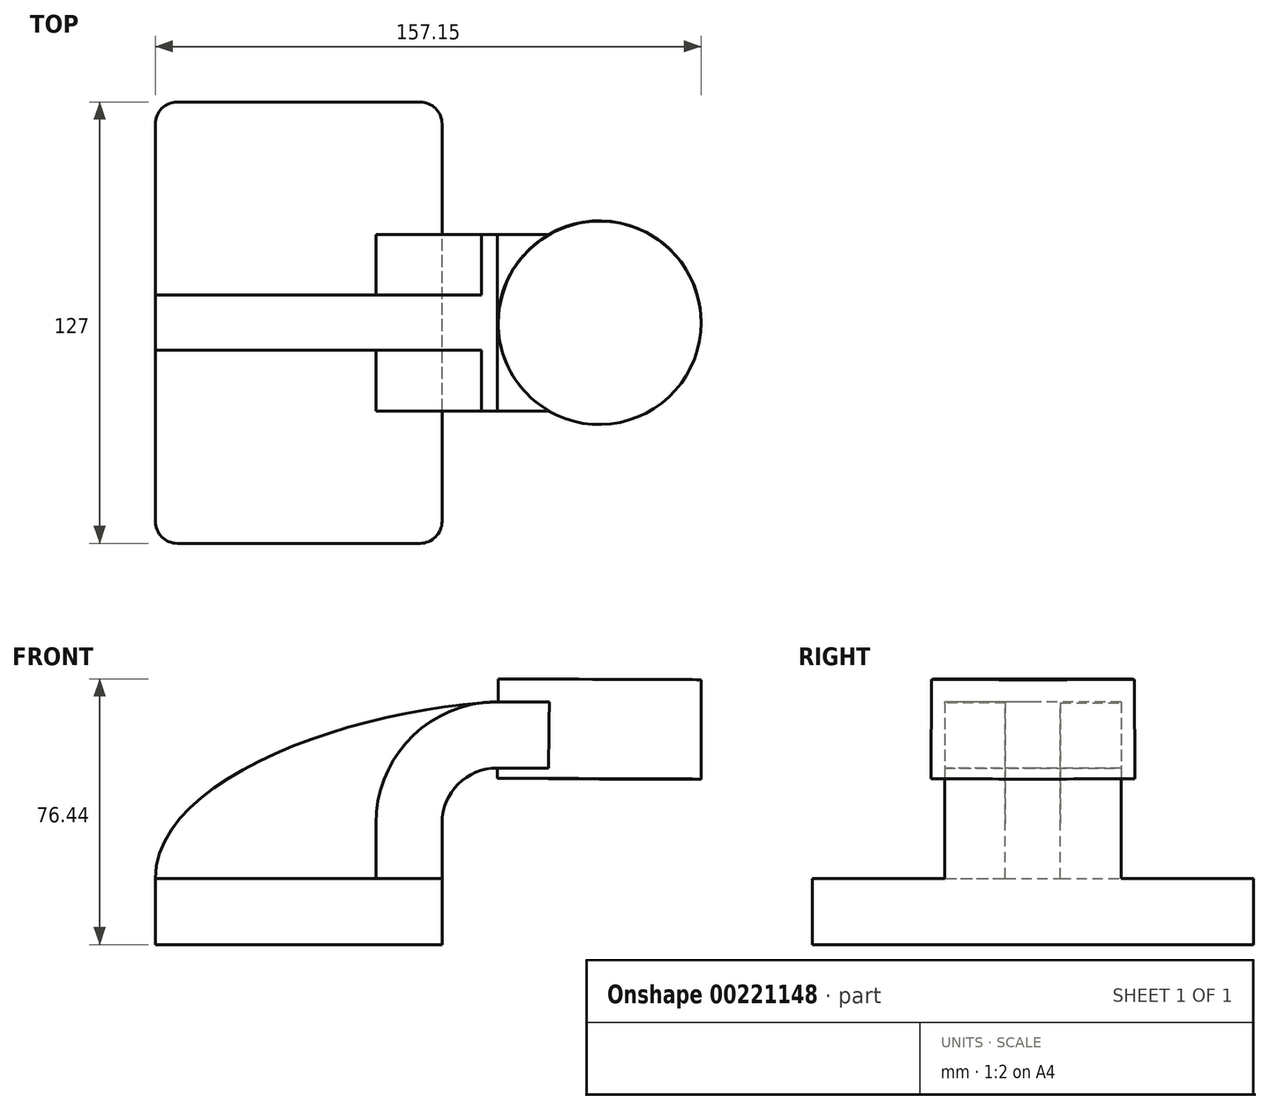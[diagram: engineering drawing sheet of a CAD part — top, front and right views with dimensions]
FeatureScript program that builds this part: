
annotation { "Feature Type Name" : "Feature", "Feature Type Description" : "" }
export const myFeature = defineFeature(function(context is Context, id is Id, definition is map)
    precondition{}
    {
        {
            var Q0;
            Q0=qCreatedBy(makeId("Front.planeOp"),FACE);
            var sketch = newSketch(context, id + "F0", { "sketchPlane" : qUnion([Q0])});
            skLineSegment(sketch, "E0.bottom", {"start": v(41.28, -9.52) * mm, "end": v(-41.28, -9.53) * mm});
            skLineSegment(sketch, "E0.top", {"start": v(41.28, 9.53) * mm, "end": v(-41.28, 9.53) * mm});
            skLineSegment(sketch, "E0.left", {"start": v(41.28, -9.52) * mm, "end": v(41.28, 9.53) * mm});
            skLineSegment(sketch, "E0.right", {"start": v(-41.28, -9.53) * mm, "end": v(-41.28, 9.53) * mm});
            skPoint(sketch, "E0.middle", {"position": v(0, 0) * mm});
            skLineSegment(sketch, "E1.bottom", {"start": v(65.07, 38.1) * mm, "end": v(115.87, 38.1) * mm});
            skLineSegment(sketch, "E1.top", {"start": v(65.07, 66.68) * mm, "end": v(115.87, 66.68) * mm});
            skLineSegment(sketch, "E1.left", {"start": v(65.07, 38.1) * mm, "end": v(65.07, 66.68) * mm});
            skLineSegment(sketch, "E1.right", {"start": v(115.87, 38.1) * mm, "end": v(115.87, 66.68) * mm});
            skPoint(sketch, "E1.middle", {"position": v(90.47, 52.39) * mm});
            skLineSegment(sketch, "E2", {"start": v(41.28, 9.53) * mm, "end": v(41.28, 25.4) * mm});
            skArc(sketch, "E3", {"start": v(41.27, 25.4) * mm, "mid": v(45.92, 36.63) * mm, "end": v(57.15, 41.28) * mm});
            skLineSegment(sketch, "E4", {"start": v(57.15, 41.28) * mm, "end": v(86.66, 41.28) * mm});
            skLineSegment(sketch, "E5.0", {"start": v(57.15, 60.33) * mm, "end": v(86.66, 60.33) * mm});
            skArc(sketch, "E5.1", {"start": v(22.23, 25.4) * mm, "mid": v(32.45, 50.1) * mm, "end": v(57.15, 60.33) * mm});
            skLineSegment(sketch, "E5.2", {"start": v(22.22, 9.53) * mm, "end": v(22.22, 25.4) * mm});
            skLineSegment(sketch, "E6", {"start": v(86.54, 38.1) * mm, "end": v(86.66, 66.68) * mm});
            skFitSpline(sketch, "E7", {"points": [v(-41.28, 9.53) * mm, v(57.15, 60.33) * mm], "startDerivative": vector(0.89, 88.77) * mm, "endDerivative": vector(120.73, 6.03) * mm});
            skSolve(sketch);
        }
        {
            var Q0;
            Q0=makeQuery(id+"F0.imprint","IMPRINT",FACE,{"disambiguationData":[TD([[makeQuery(id+"F0.imprint","IMPRINT",EDGE,{"derivedFrom":sQuery(id+"F0.wireOp",EDGE,"E0.bottom")}),-1.0]])]});
            extrude(context, id + "F1", {"entities" : qUnion([Q0]), "endBound" : BoundingType.SYMMETRIC, "depth" : 127 * mm});
        }
        {
            var Q0;
            {var subQ1=sQuery(id+"F0.wireOp",EDGE,"E2");Q0=makeQuery(id+"F0.imprint","IMPRINT",FACE,{"disambiguationData":[TD([[makeQuery(id+"F0.imprint","IMPRINT",EDGE,{"derivedFrom":subQ1}),1.0]])]});}
            var Q1;
            {var subQ0=sQuery(id+"F0.wireOp",EDGE,"E4");var subQ1=sQuery(id+"F0.wireOp",EDGE,"E1.left");var subQ2=makeQuery(id+"F0.imprint","INTERSECT",VERTEX,{"derivedFrom":[subQ1,subQ0]});Q1=makeQuery(id+"F0.imprint","IMPRINT",FACE,{"disambiguationData":[TD([[makeQuery(id+"F0.imprint","IMPRINT",EDGE,{"disambiguationData":[TD([[subQ2,-1.0]])],"derivedFrom":subQ1}),-1.0]])]});}
            extrude(context, id + "F2", {"entities" : qUnion([Q0, Q1]), "operationType" : NewBodyOperationType.ADD, "endBound" : BoundingType.SYMMETRIC, "depth" : 50.8 * mm});
        }
        {
            var Q0;
            {var subQ3=sQuery(id+"F0.wireOp",EDGE,"E5.2");Q0=makeQuery(id+"F0.imprint","IMPRINT",FACE,{"disambiguationData":[TD([[makeQuery(id+"F0.imprint","IMPRINT",EDGE,{"derivedFrom":subQ3}),1.0]])]});}
            extrude(context, id + "F3", {"entities" : qUnion([Q0]), "operationType" : NewBodyOperationType.ADD, "endBound" : BoundingType.SYMMETRIC, "depth" : 15.88 * mm});
        }
        {
            var Q0;
            {var subQ0=sQuery(id+"F0.wireOp",EDGE,"E1.right");Q0=makeQuery(id+"F0.imprint","IMPRINT",FACE,{"disambiguationData":[TD([[makeQuery(id+"F0.imprint","IMPRINT",EDGE,{"derivedFrom":subQ0}),1.0]])]});}
            var Q1;
            Q1=sQuery(id+"F0.wireOp",EDGE,"E6");
            revolve(context, id + "F4", {"operationType" : NewBodyOperationType.ADD, "entities" : qUnion([Q0]), "axis" : qUnion([Q1]), "revolveType" : RevolveType.FULL});
        }
        {
            var Q0;
            Q0=makeQuery(id+"F1.opExtrude","CAP_EDGE",EDGE,{"disambiguationData":[OSD([sQuery(id+"F0.wireOp",EDGE,"E0.left")])],"isStart":false});
            var Q1;
            Q1=makeQuery(id+"F1.opExtrude","CAP_EDGE",EDGE,{"disambiguationData":[OSD([sQuery(id+"F0.wireOp",EDGE,"E0.left")])],"isStart":true});
            var Q2;
            Q2=makeQuery(id+"F1.opExtrude","CAP_EDGE",EDGE,{"disambiguationData":[OSD([sQuery(id+"F0.wireOp",EDGE,"E0.right")])],"isStart":false});
            var Q3;
            Q3=makeQuery(id+"F1.opExtrude","CAP_EDGE",EDGE,{"disambiguationData":[OSD([sQuery(id+"F0.wireOp",EDGE,"E0.right")])],"isStart":true});
            fillet(context, id + "F5", {"entities" : qUnion([Q0, Q1, Q2, Q3]), "radius" : 6.35 * mm, "tangentPropagation" : true, "allowEdgeOverflow" : false});
        }
    });
